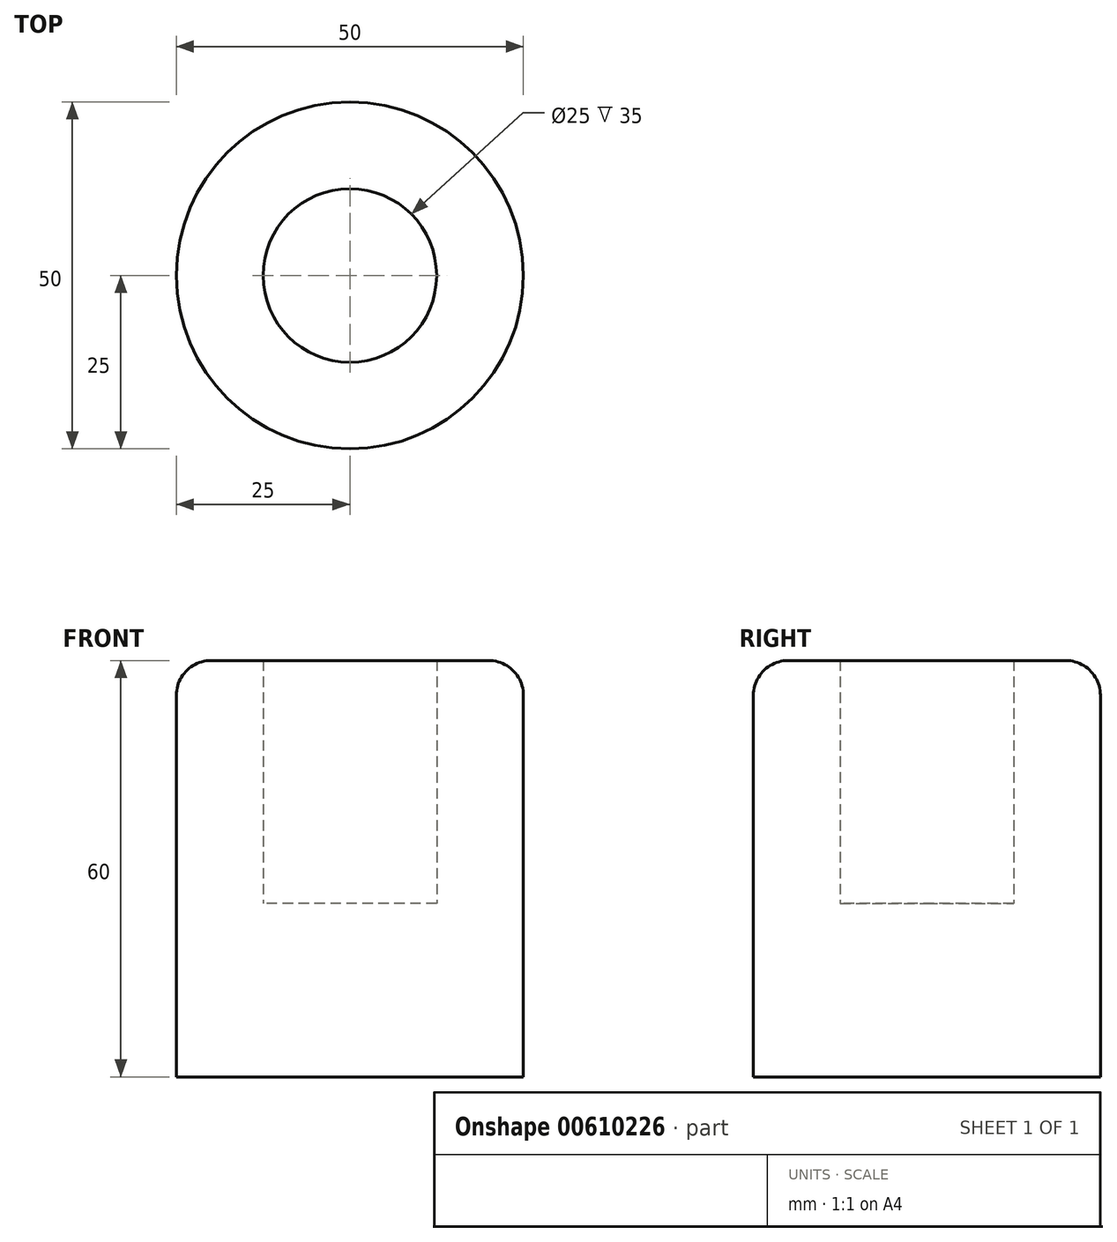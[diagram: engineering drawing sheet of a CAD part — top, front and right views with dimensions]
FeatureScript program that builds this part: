
annotation { "Feature Type Name" : "Feature", "Feature Type Description" : "" }
export const myFeature = defineFeature(function(context is Context, id is Id, definition is map)
    precondition{}
    {
        {
            var Q0;
            Q0=qCreatedBy(makeId("Top.planeOp"),FACE);
            var sketch = newSketch(context, id + "F0", { "sketchPlane" : qUnion([Q0])});
            skCircle(sketch, "E0", {"center": v(0, 0) * mm, "radius": 25 * mm});
            skCircle(sketch, "E1", {"center": v(0, 0) * mm, "radius": 12.5 * mm});
            skSolve(sketch);
        }
        {
            var Q0;
            Q0=makeQuery(id+"F0.imprint","IMPRINT",FACE,{"disambiguationData":[TD([[makeQuery(id+"F0.imprint","IMPRINT",EDGE,{"derivedFrom":sQuery(id+"F0.wireOp",EDGE,"E1")}),1.0]])]});
            extrude(context, id + "F1", {"entities" : qUnion([Q0]), "depth" : 25 * mm, "offsetDistance" : 25 * mm});
        }
        {
            var Q0;
            Q0 = qSketchRegion(id + "F0", true);
            extrude(context, id + "F2", {"entities" : qUnion([Q0]), "operationType" : NewBodyOperationType.ADD, "depth" : 60 * mm, "offsetDistance" : 25 * mm});
        }
        {
            var Q0;
            Q0=makeQuery(id+"F2.opExtrude","CAP_EDGE",EDGE,{"disambiguationData":[OSD([sQuery(id+"F0.wireOp",EDGE,"E0")])],"isStart":false});
            fillet(context, id + "F3", {"entities" : qUnion([Q0]), "radius" : 5 * mm, "tangentPropagation" : true, "allowEdgeOverflow" : false});
        }
    });
